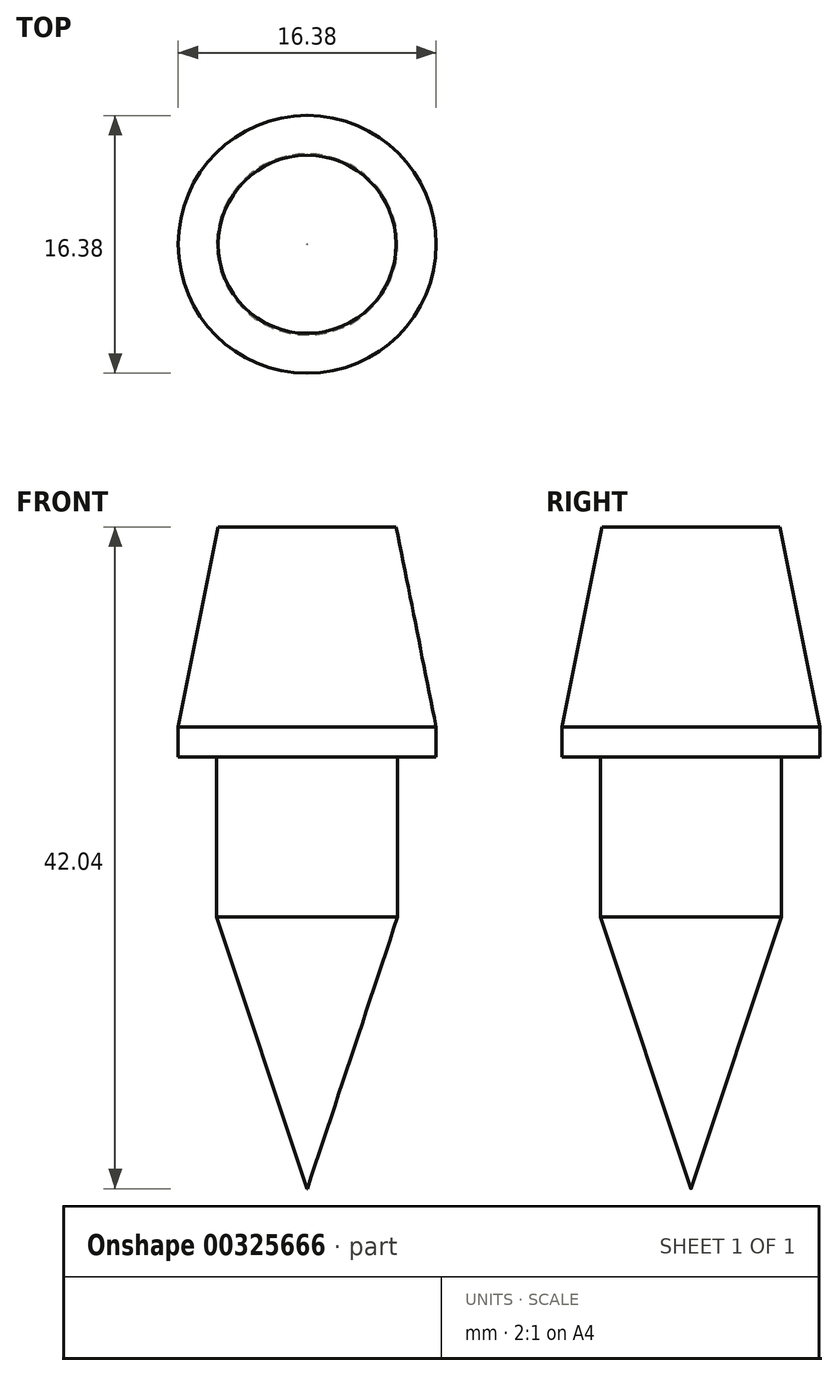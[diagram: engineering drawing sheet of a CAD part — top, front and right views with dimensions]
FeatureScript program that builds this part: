
annotation { "Feature Type Name" : "Feature", "Feature Type Description" : "" }
export const myFeature = defineFeature(function(context is Context, id is Id, definition is map)
    precondition{}
    {
        {
            var Q0;
            Q0=qCreatedBy(makeId("Top.planeOp"),FACE);
            var sketch = newSketch(context, id + "F0", { "sketchPlane" : qUnion([Q0])});
            skCircle(sketch, "E0", {"center": v(0, 0) * mm, "radius": 5.75 * mm});
            skSolve(sketch);
        }
        {
            var Q0;
            Q0=makeQuery(id+"F0.imprint","IMPRINT",FACE,{"disambiguationData":[TD([[makeQuery(id+"F0.imprint","IMPRINT",EDGE,{"derivedFrom":sQuery(id+"F0.wireOp",EDGE,"E0")}),1.0]])]});
            extrude(context, id + "F1", {"entities" : qUnion([Q0]), "depth" : 10.16 * mm});
        }
        {
            var Q0;
            Q0=makeQuery(id+"F1.opExtrude","CAP_FACE",FACE,{"disambiguationData":[OSD([sQuery(id+"F0.wireOp",EDGE,"E0")])],"isStart":false});
            var sketch = newSketch(context, id + "F2", { "sketchPlane" : qUnion([Q0])});
            skCircle(sketch, "E1", {"center": v(0, 0) * mm, "radius": 8.2 * mm});
            skSolve(sketch);
        }
        {
            var Q0;
            Q0=makeQuery(id+"F2.imprint","IMPRINT",FACE,{"disambiguationData":[TD([[makeQuery(id+"F2.imprint","IMPRINT",EDGE,{"derivedFrom":makeQuery(id+"F1.opExtrude","CAP_EDGE",EDGE,{"disambiguationData":[OSD([sQuery(id+"F0.wireOp",EDGE,"E0")])],"isStart":false})}),1.0]])]});
            var Q1;
            Q1=makeQuery(id+"F2.imprint","IMPRINT",FACE,{"disambiguationData":[TD([[makeQuery(id+"F2.imprint","IMPRINT",EDGE,{"derivedFrom":sQuery(id+"F2.wireOp",EDGE,"E1")}),1.0]])]});
            extrude(context, id + "F3", {"entities" : qUnion([Q0, Q1]), "operationType" : NewBodyOperationType.ADD, "depth" : 1.9 * mm});
        }
        {
            var Q0;
            Q0=makeQuery(id+"F3.opExtrude","CAP_FACE",FACE,{"disambiguationData":[OSD([sQuery(id+"F2.wireOp",EDGE,"E1")])],"isStart":false});
            var sketch = newSketch(context, id + "F4", { "sketchPlane" : qUnion([Q0])});
            skSolve(sketch);
        }
        {
            var Q0;
            Q0=makeQuery(id+"F4.imprint","IMPRINT",FACE,{"disambiguationData":[TD([[makeQuery(id+"F4.imprint","IMPRINT",EDGE,{"derivedFrom":makeQuery(id+"F3.opExtrude","CAP_EDGE",EDGE,{"disambiguationData":[OSD([sQuery(id+"F2.wireOp",EDGE,"E1")])],"isStart":false})}),1.0]])]});
            extrude(context, id + "F5", {"entities" : qUnion([Q0]), "operationType" : NewBodyOperationType.ADD, "depth" : 12.7 * mm});
        }
        {
            var Q0;
            Q0=makeQuery(id+"F5.opExtrude","CAP_EDGE",EDGE,{"disambiguationData":[OSD([sQuery(id+"F2.wireOp",EDGE,"E1")])],"isStart":false});
            chamfer(context, id + "F6", {"entities" : qUnion([Q0]), "chamferType" : ChamferType.TWO_OFFSETS, "width1" : 2.54 * mm, "oppositeDirection" : false, "width2" : 12.7 * mm, "tangentPropagation" : true});
        }
        {
            var Q0;
            Q0=makeQuery(id+"F1.opExtrude","CAP_FACE",FACE,{"disambiguationData":[OSD([sQuery(id+"F0.wireOp",EDGE,"E0")])],"isStart":true});
            extrude(context, id + "F7", {"entities" : qUnion([Q0]), "operationType" : NewBodyOperationType.ADD, "depth" : 17.27 * mm});
        }
        {
            var Q0;
            Q0=makeQuery(id+"F7.opExtrude","CAP_EDGE",EDGE,{"disambiguationData":[OSD([sQuery(id+"F0.wireOp",EDGE,"E0")])],"isStart":false});
            chamfer(context, id + "F8", {"entities" : qUnion([Q0]), "chamferType" : ChamferType.TWO_OFFSETS, "width1" : 17.27 * mm, "oppositeDirection" : false, "width2" : 5.74 * mm, "tangentPropagation" : true});
        }
    });
